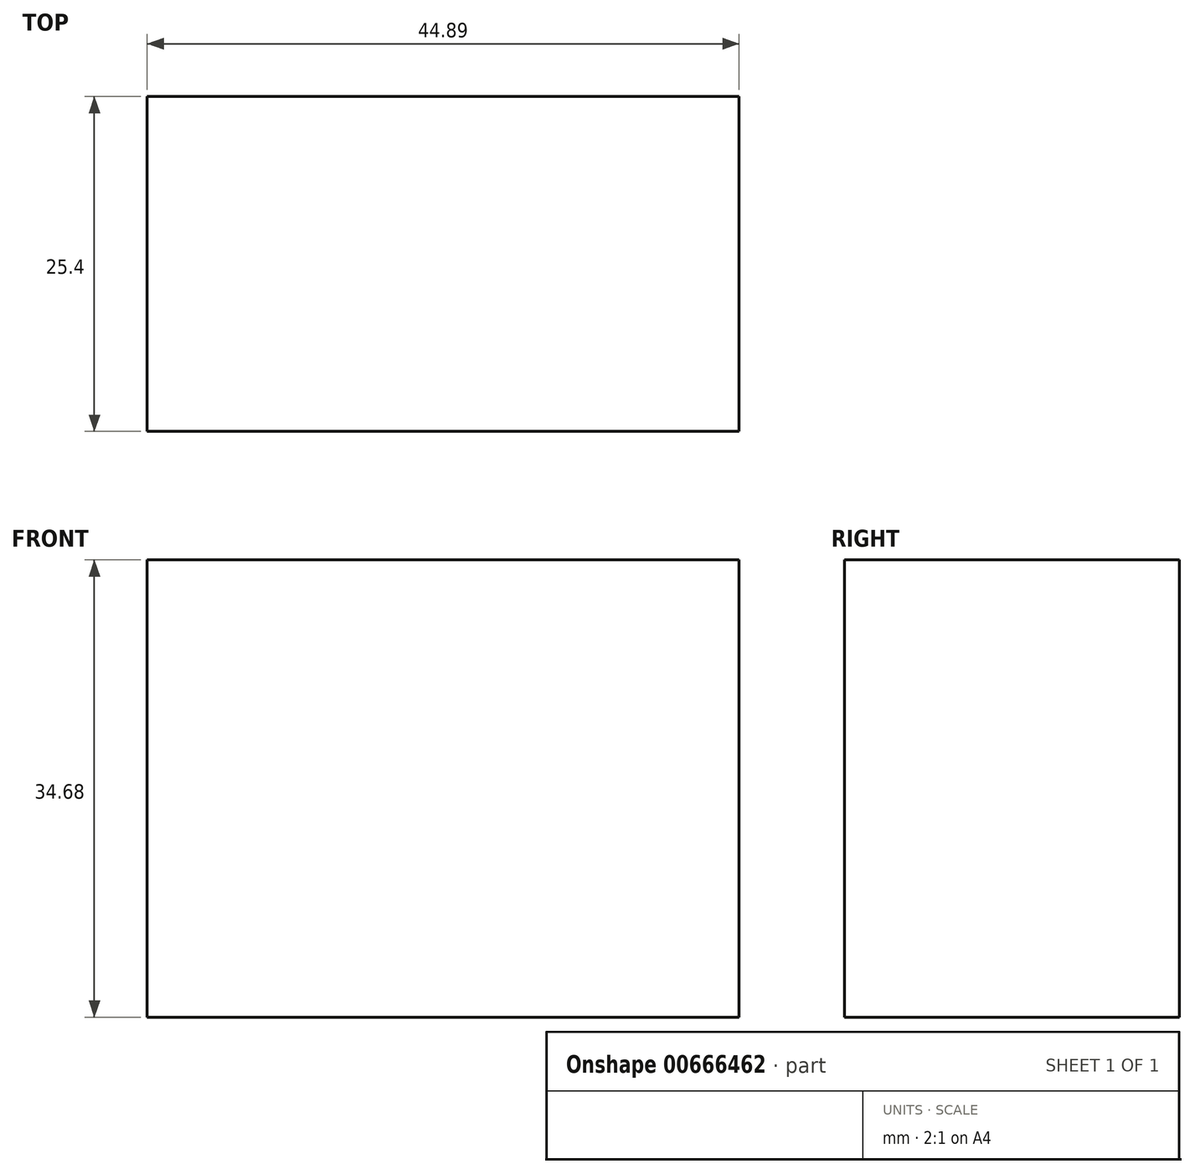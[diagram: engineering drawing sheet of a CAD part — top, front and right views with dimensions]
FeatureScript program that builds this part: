
annotation { "Feature Type Name" : "Feature", "Feature Type Description" : "" }
export const myFeature = defineFeature(function(context is Context, id is Id, definition is map)
    precondition{}
    {
        {
            var Q0;
            Q0=qCreatedBy(makeId("Front.planeOp"),FACE);
            var sketch = newSketch(context, id + "F0", { "sketchPlane" : qUnion([Q0])});
            skLineSegment(sketch, "E0.bottom", {"start": v(0, 0) * mm, "end": v(44.9, 0) * mm});
            skLineSegment(sketch, "E0.top", {"start": v(0, -34.68) * mm, "end": v(44.9, -34.68) * mm});
            skLineSegment(sketch, "E0.left", {"start": v(0, 0) * mm, "end": v(0, -34.68) * mm});
            skLineSegment(sketch, "E0.right", {"start": v(44.9, 0) * mm, "end": v(44.9, -34.68) * mm});
            skSolve(sketch);
        }
        {
            var Q0;
            Q0=makeQuery(id+"F0.imprint","IMPRINT",FACE,{"disambiguationData":[TD([[makeQuery(id+"F0.imprint","IMPRINT",EDGE,{"derivedFrom":sQuery(id+"F0.wireOp",EDGE,"E0.bottom")}),-1.0]])]});
            extrude(context, id + "F1", {"entities" : qUnion([Q0]), "depth" : 25.4 * mm, "offsetDistance" : 25.4 * mm});
        }
        {
            var Q0;
            Q0=makeQuery(id+"F1.opExtrude","CAP_FACE",FACE,{"disambiguationData":[OSD([sQuery(id+"F0.wireOp",EDGE,"E0.bottom"),sQuery(id+"F0.wireOp",EDGE,"E0.top"),sQuery(id+"F0.wireOp",EDGE,"E0.left"),sQuery(id+"F0.wireOp",EDGE,"E0.right")])],"isStart":false});
            var sketch = newSketch(context, id + "F2", { "sketchPlane" : qUnion([Q0])});
            skCircle(sketch, "E1", {"center": v(26.94, -6.64) * mm, "radius": 5.4 * mm});
            skSolve(sketch);
        }
        {
            var Q0;
            Q0=sQuery(id+"F2.wireOp",EDGE,"E1");
            extrude(context, id + "F3", {"bodyType" : ToolBodyType.SURFACE, "surfaceEntities" : qUnion([Q0]), "depth" : 12.7 * mm, "offsetDistance" : 25.4 * mm});
        }
    });
